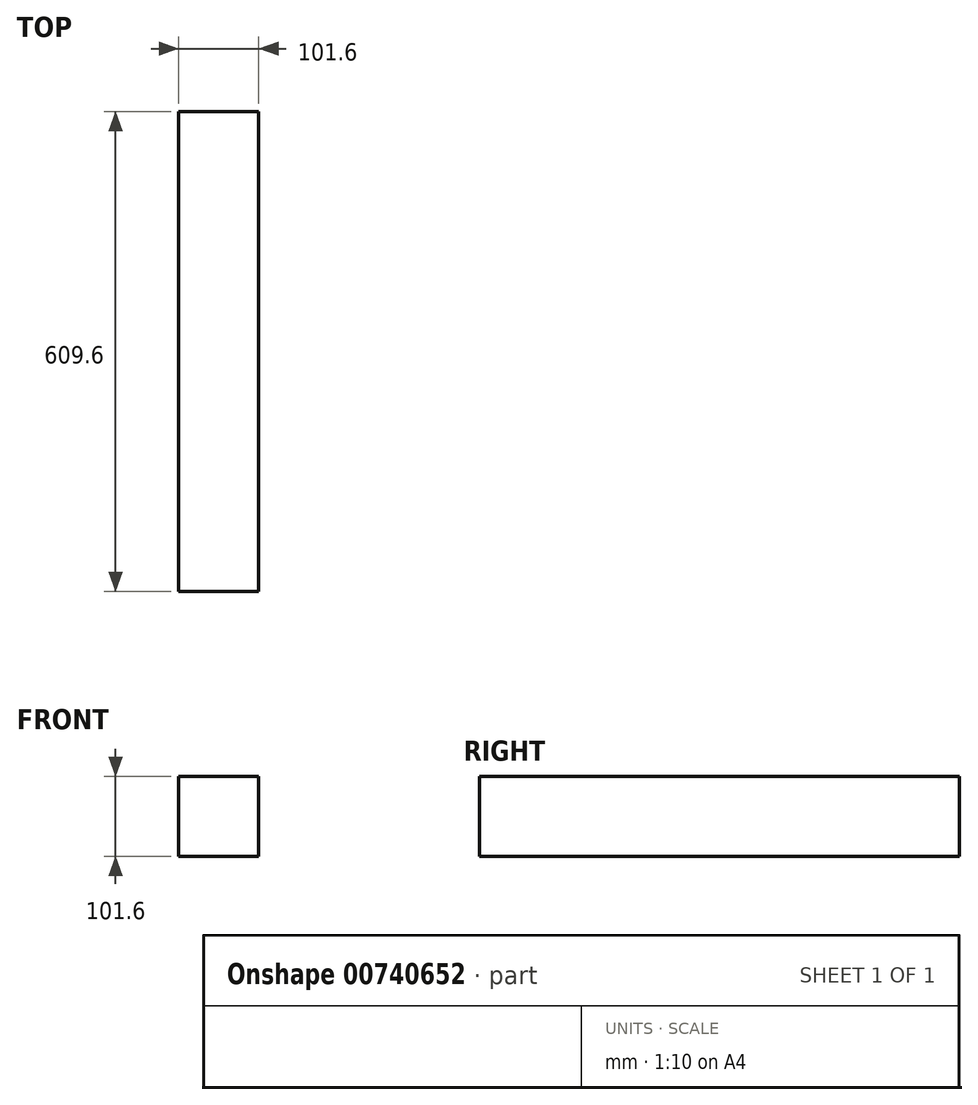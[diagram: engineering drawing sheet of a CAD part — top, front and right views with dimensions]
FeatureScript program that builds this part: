
annotation { "Feature Type Name" : "Feature", "Feature Type Description" : "" }
export const myFeature = defineFeature(function(context is Context, id is Id, definition is map)
    precondition{}
    {
        {
            var Q0;
            Q0=qCreatedBy(makeId("Front.planeOp"),FACE);
            var sketch = newSketch(context, id + "F0", { "sketchPlane" : qUnion([Q0])});
            skLineSegment(sketch, "E0.bottom", {"start": v(0, 0) * mm, "end": v(101.6, 0) * mm});
            skLineSegment(sketch, "E0.top", {"start": v(0, 101.6) * mm, "end": v(101.6, 101.6) * mm});
            skLineSegment(sketch, "E0.left", {"start": v(0, 0) * mm, "end": v(0, 101.6) * mm});
            skLineSegment(sketch, "E0.right", {"start": v(101.6, 0) * mm, "end": v(101.6, 101.6) * mm});
            skSolve(sketch);
        }
        {
            var Q0;
            Q0 = qSketchRegion(id + "F0", true);
            extrude(context, id + "F1", {"entities" : qUnion([Q0]), "depth" : 609.6 * mm, "offsetDistance" : 25.4 * mm});
        }
    });
